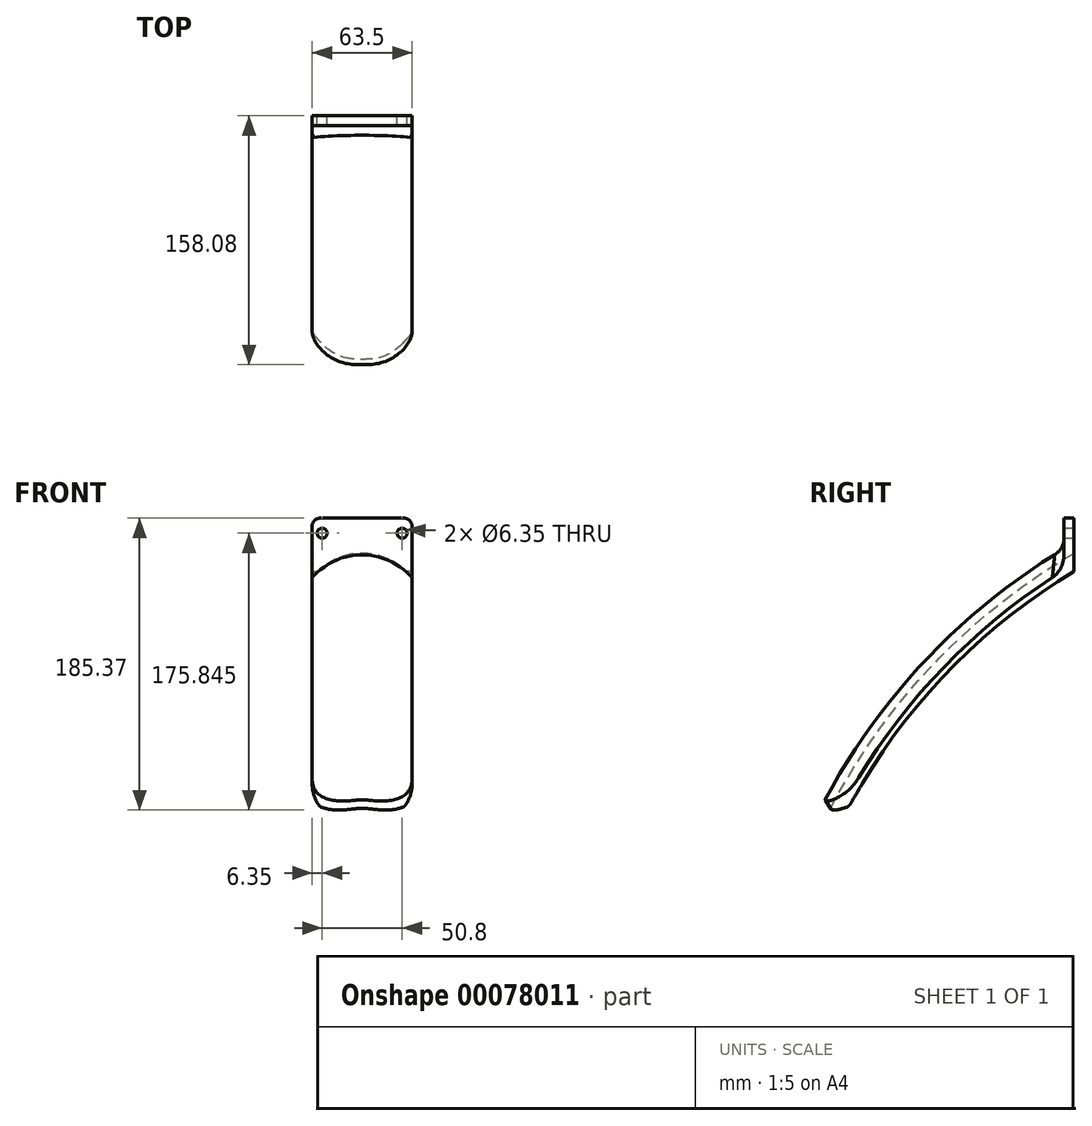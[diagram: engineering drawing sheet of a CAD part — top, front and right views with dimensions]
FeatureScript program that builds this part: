
annotation { "Feature Type Name" : "Feature", "Feature Type Description" : "" }
export const myFeature = defineFeature(function(context is Context, id is Id, definition is map)
    precondition{}
    {
        {
            var Q0;
            Q0=qCreatedBy(makeId("Right.planeOp"),FACE);
            var sketch = newSketch(context, id + "F0", { "sketchPlane" : qUnion([Q0])});
            skCircle(sketch, "E0", {"center": v(203.2, -351.95) * mm, "radius": 342.9 * mm});
            skLineSegment(sketch, "E1", {"start": v(203.2, -351.95) * mm, "end": v(-156.39, -162.6) * mm, "construction": true});
            skLineSegment(sketch, "E2", {"start": v(203.2, -351.95) * mm, "end": v(0, 0) * mm, "construction": true});
            skLineSegment(sketch, "E3", {"start": v(203.2, -351.95) * mm, "end": v(-203.2, -351.95) * mm, "construction": true});
            skArc(sketch, "E4", {"start": v(-156.39, -162.6) * mm, "mid": v(496.1, -633.68) * mm, "end": v(0, 0) * mm});
            skArc(sketch, "E5", {"start": v(0, 0) * mm, "mid": v(-89.7, -70.23) * mm, "end": v(-156.39, -162.6) * mm});
            skSolve(sketch);
        }
        {
            var Q0;
            Q0=qCreatedBy(makeId("Front.planeOp"),FACE);
            var sketch = newSketch(context, id + "F1", { "sketchPlane" : qUnion([Q0])});
            skLineSegment(sketch, "E6.bottom", {"start": v(-31.75, 19.05) * mm, "end": v(31.75, 19.05) * mm});
            skLineSegment(sketch, "E6.top", {"start": v(-31.75, 0) * mm, "end": v(31.75, 0) * mm, "construction": true});
            skLineSegment(sketch, "E6.left", {"start": v(-31.75, 19.05) * mm, "end": v(-31.75, 0) * mm});
            skLineSegment(sketch, "E6.right", {"start": v(31.75, 19.05) * mm, "end": v(31.75, 0) * mm});
            skPoint(sketch, "E6.middle", {"position": v(0, 9.52) * mm});
            skLineSegment(sketch, "E7", {"start": v(-25.4, 9.53) * mm, "end": v(25.4, 9.52) * mm, "construction": true});
            skArc(sketch, "E8", {"start": v(28.57, -11.5) * mm, "mid": v(0, 0) * mm, "end": v(-28.57, -11.5) * mm, "construction": true});
            skArc(sketch, "E9.0.startCap", {"start": v(30.77, -9.2) * mm, "mid": v(30.87, -13.69) * mm, "end": v(26.38, -13.78) * mm});
            skArc(sketch, "E9.0.endCap", {"start": v(-26.38, -13.78) * mm, "mid": v(-30.87, -13.69) * mm, "end": v(-30.77, -9.2) * mm});
            skArc(sketch, "E9.0.left", {"start": v(26.38, -13.78) * mm, "mid": v(0, -3.17) * mm, "end": v(-26.38, -13.78) * mm});
            skArc(sketch, "E9.0.right", {"start": v(30.77, -9.2) * mm, "mid": v(0, 3.18) * mm, "end": v(-30.77, -9.2) * mm});
            skLineSegment(sketch, "E10", {"start": v(-31.75, 0) * mm, "end": v(-31.75, -11.5) * mm});
            skLineSegment(sketch, "E11", {"start": v(31.75, 0) * mm, "end": v(31.75, -11.5) * mm});
            skLineSegment(sketch, "E12", {"start": v(-31.75, -11.5) * mm, "end": v(-31.75, -14.67) * mm});
            skLineSegment(sketch, "E13", {"start": v(-31.75, -14.67) * mm, "end": v(-28.57, -14.67) * mm});
            skLineSegment(sketch, "E14", {"start": v(0, 9.52) * mm, "end": v(0, 0) * mm, "construction": true});
            skLineSegment(sketch, "E15.MirrorCS", {"start": v(31.75, -11.5) * mm, "end": v(31.75, -14.67) * mm});
            skLineSegment(sketch, "E16.MirrorCS", {"start": v(31.75, -14.67) * mm, "end": v(28.58, -14.67) * mm});
            skLineSegment(sketch, "E17", {"start": v(-30.77, -9.2) * mm, "end": v(-31.75, -10.14) * mm});
            skLineSegment(sketch, "E18.MirrorCS", {"start": v(30.77, -9.2) * mm, "end": v(31.75, -10.14) * mm});
            skSolve(sketch);
        }
        {
            var Q0;
            {var subQ0=sQuery(id+"F1.wireOp",EDGE,"E9.0.left");Q0=makeQuery(id+"F1.imprint","IMPRINT",FACE,{"disambiguationData":[TD([[makeQuery(id+"F1.imprint","IMPRINT",EDGE,{"derivedFrom":subQ0}),-1.0]])]});}
            var Q1;
            {var subQ0=sQuery(id+"F1.wireOp",EDGE,"E12");Q1=makeQuery(id+"F1.imprint","IMPRINT",FACE,{"disambiguationData":[TD([[makeQuery(id+"F1.imprint","IMPRINT",EDGE,{"derivedFrom":subQ0}),1.0]])]});}
            var Q2;
            {var subQ0=sQuery(id+"F1.wireOp",EDGE,"E17");Q2=makeQuery(id+"F1.imprint","IMPRINT",FACE,{"disambiguationData":[TD([[makeQuery(id+"F1.imprint","IMPRINT",EDGE,{"derivedFrom":subQ0}),1.0]])]});}
            var Q3;
            {var subQ0=sQuery(id+"F1.wireOp",EDGE,"E15.MirrorCS");Q3=makeQuery(id+"F1.imprint","IMPRINT",FACE,{"disambiguationData":[TD([[makeQuery(id+"F1.imprint","IMPRINT",EDGE,{"derivedFrom":subQ0}),-1.0]])]});}
            var Q4;
            {var subQ0=sQuery(id+"F1.wireOp",EDGE,"E18.MirrorCS");Q4=makeQuery(id+"F1.imprint","IMPRINT",FACE,{"disambiguationData":[TD([[makeQuery(id+"F1.imprint","IMPRINT",EDGE,{"derivedFrom":subQ0}),-1.0]])]});}
            var Q5;
            Q5=sQuery(id+"F0.wireOp",EDGE,"E5");
            sweep(context, id + "F2", {"profiles" : qUnion([Q0, Q1, Q2, Q3, Q4]), "path" : qUnion([Q5])});
        }
        {
            var Q0;
            Q0 = qSketchRegion(id + "F1", true);
            extrude(context, id + "F3", {"entities" : qUnion([Q0]), "operationType" : NewBodyOperationType.ADD, "depth" : 6.35 * mm});
        }
        {
            var Q0;
            Q0=sQuery(id+"F1.wireOp",VERTEX,"E7.start");
            var Q1;
            Q1=sQuery(id+"F1.wireOp",VERTEX,"E7.end");
            var Q2;
            Q2=makeQuery(id+"F2.opSweep","SWEPT_BODY",BODY,{"disambiguationData":[OSD([sQuery(id+"F0.wireOp",EDGE,"E5"),sQuery(id+"F1.wireOp",EDGE,"E9.0.startCap"),sQuery(id+"F1.wireOp",EDGE,"E9.0.endCap"),sQuery(id+"F1.wireOp",EDGE,"E9.0.left"),sQuery(id+"F1.wireOp",EDGE,"E9.0.right")])]});
            hole(context, id + "F4", {"style" : HoleStyle.SIMPLE, "endStyle" : HoleEndStyle.THROUGH, "oppositeDirection" : true, "holeDiameter" : 6.35 * mm, "locations" : qUnion([Q0, Q1]), "scope" : qUnion([Q2]), "isTappedThrough" : true});
        }
        {
            var Q0;
            Q0=makeQuery(id+"F3.opExtrude","SWEPT_EDGE",EDGE,{"disambiguationData":[OSD([sQuery(id+"F1.wireOp",EDGE,"E6.bottom"),sQuery(id+"F1.wireOp",EDGE,"E6.left")])]});
            var Q1;
            Q1=makeQuery(id+"F3.opExtrude","SWEPT_EDGE",EDGE,{"disambiguationData":[OSD([sQuery(id+"F1.wireOp",EDGE,"E6.bottom"),sQuery(id+"F1.wireOp",EDGE,"E6.right")])]});
            fillet(context, id + "F5", {"entities" : qUnion([Q0, Q1]), "radius" : 5.08 * mm, "tangentPropagation" : true, "allowEdgeOverflow" : false});
        }
        {
            var Q0;
            Q0=makeQuery(id+"F3.boolean.opBoolean","INTERSECT",EDGE,{"derivedFrom":[makeQuery(id+"F2.opSweep","SWEPT_FACE",FACE,{"disambiguationData":[OSD([sQuery(id+"F0.wireOp",EDGE,"E5"),sQuery(id+"F1.wireOp",EDGE,"E9.0.right")])]}),makeQuery(id+"F3.opExtrude","CAP_FACE",FACE,{"disambiguationData":[OSD([sQuery(id+"F1.wireOp",EDGE,"E6.bottom"),sQuery(id+"F1.wireOp",EDGE,"E6.left"),sQuery(id+"F1.wireOp",EDGE,"E6.right"),sQuery(id+"F1.wireOp",EDGE,"E9.0.startCap"),sQuery(id+"F1.wireOp",EDGE,"E9.0.endCap"),sQuery(id+"F1.wireOp",EDGE,"E9.0.left"),sQuery(id+"F1.wireOp",EDGE,"E10"),sQuery(id+"F1.wireOp",EDGE,"E11")])],"isStart":false})]});
            fillet(context, id + "F6", {"entities" : qUnion([Q0]), "radius" : 12.7 * mm, "tangentPropagation" : true, "allowEdgeOverflow" : false});
        }
        {
            var Q0;
            Q0=makeQuery(id+"F2.opSweep","CAP_EDGE",EDGE,{"disambiguationData":[OSD([sQuery(id+"F0.wireOp",VERTEX,"E5.end"),sQuery(id+"F1.wireOp",EDGE,"E11"),sQuery(id+"F1.wireOp",EDGE,"E15.MirrorCS")])],"isStart":false});
            var Q1;
            Q1=makeQuery(id+"F2.opSweep","CAP_EDGE",EDGE,{"disambiguationData":[OSD([sQuery(id+"F0.wireOp",VERTEX,"E5.end"),sQuery(id+"F1.wireOp",EDGE,"E10"),sQuery(id+"F1.wireOp",EDGE,"E12")])],"isStart":false});
            fillet(context, id + "F7", {"entities" : qUnion([Q0, Q1]), "radius" : 25.4 * mm, "tangentPropagation" : true, "allowEdgeOverflow" : false});
        }
    });
